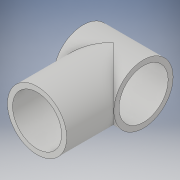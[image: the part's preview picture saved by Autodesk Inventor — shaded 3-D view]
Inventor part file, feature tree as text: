
AUTODESK INVENTOR PART (.ipt)
format: ipt  version: 2018 (Build 220112000, 112)  size: 124,416 bytes
history: native  units: in
note: dims shown in document units (in); Inventor stores cm internally (conversion verified against a paired STEP export)
features: sketch x5, extrude x4, plane x2
ambient origin geometry x8: Origin, YZ Plane, XZ Plane, XY Plane, X Axis, Y Axis, Z Axis, Center Point
bodies: Solid1 (feature_tree)
feature tree (11):
  sketch  "Sketch1"  dims[d1=1.595in d2=-0.8125in d3=2.0495in d4=0.0in]
  sketch  "Sketch2"  dims[d5=1.321in d10=1.321in]
  plane  "Work Plane2"
  extrude  "Extrusion1"  Depth=2.0495in TaperAngle=0.0deg
  sketch  "Sketch3"  dims[d11=1.625in d12=0.0in d13=1.625in d14=0.0in]
  sketch  "Sketch4"  dims[d15=1.256in d16=0.0in]
  sketch  "Sketch5"
  extrude  "Extrusion2"  Depth=1.321in
  extrude  "Extrusion3"  Depth=1.625in TaperAngle=0.0deg
  extrude  "Extrusion4"  [1 undecoded]
  plane  "Work Plane1"
note: 1 required parameter value undecoded (feature->parameter linkage not recoverable at this tier; creation-order binding heuristic only, values carry confidence <= 0.55)
